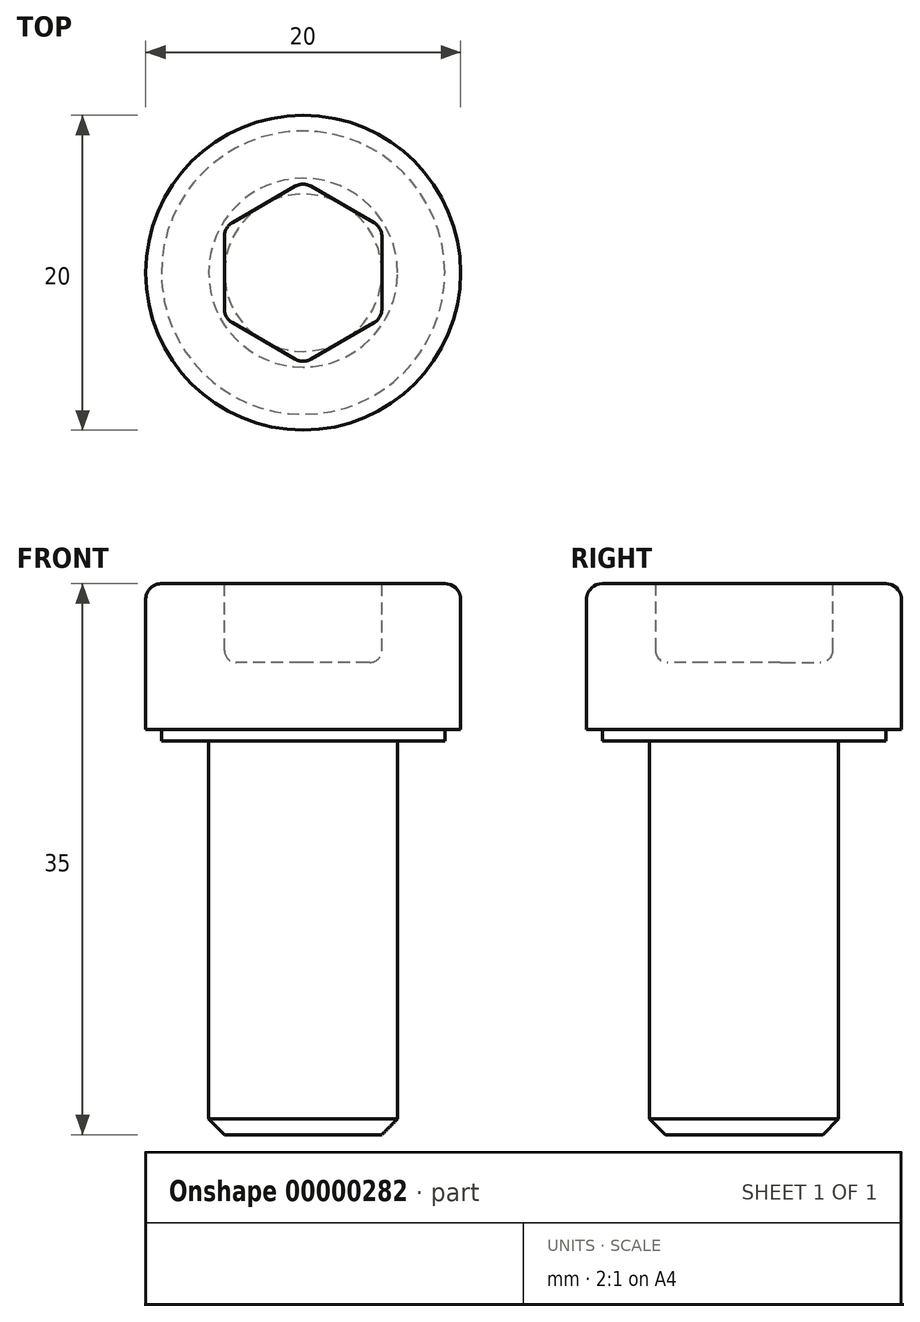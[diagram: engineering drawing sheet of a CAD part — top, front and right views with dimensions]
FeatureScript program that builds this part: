
annotation { "Feature Type Name" : "Feature", "Feature Type Description" : "" }
export const myFeature = defineFeature(function(context is Context, id is Id, definition is map)
    precondition{}
    {
        {
            var Q0;
            Q0 = qCreatedBy(makeId("Front.planeOp"), FACE);
            var sketch = newSketch(context, id + "F0", { "sketchPlane" : qUnion([Q0])});
            skLineSegment(sketch, "E0", {"start": v(-6, 0) * mm, "end": v(-9, 0) * mm});
            skLineSegment(sketch, "E1", {"start": v(-9, 0) * mm, "end": v(-9, 0.75) * mm});
            skLineSegment(sketch, "E2", {"start": v(-9, 0.75) * mm, "end": v(-10, 0.75) * mm});
            skLineSegment(sketch, "E3", {"start": v(-10, 0.75) * mm, "end": v(-10, 10) * mm});
            skLineSegment(sketch, "E4", {"start": v(-10, 10) * mm, "end": v(0, 10) * mm});
            skLineSegment(sketch, "E5", {"start": v(0, 10) * mm, "end": v(0, -25) * mm});
            skLineSegment(sketch, "E6", {"start": v(0, -25) * mm, "end": v(-6, -25) * mm});
            skLineSegment(sketch, "E7", {"start": v(-6, -25) * mm, "end": v(-6, 0) * mm});
            skLineSegment(sketch, "E8", {"start": v(0, -25) * mm, "end": v(0, -26.5) * mm, "construction": true});
            skLineSegment(sketch, "E9.0.MirrorCS", {"start": v(0, -25) * mm, "end": v(6, -25) * mm, "construction": true});
            skLineSegment(sketch, "E10.0.MirrorCS", {"start": v(6, -25) * mm, "end": v(6, 0) * mm, "construction": true});
            skLineSegment(sketch, "E11.0.MirrorCS", {"start": v(6, 0) * mm, "end": v(9, 0) * mm, "construction": true});
            skLineSegment(sketch, "E12.0.MirrorCS", {"start": v(9, 0) * mm, "end": v(9, 0.75) * mm, "construction": true});
            skLineSegment(sketch, "E13.0.MirrorCS", {"start": v(9, 0.75) * mm, "end": v(10, 0.75) * mm, "construction": true});
            skLineSegment(sketch, "E14.0.MirrorCS", {"start": v(10, 0.75) * mm, "end": v(10, 10) * mm, "construction": true});
            skLineSegment(sketch, "E15.0.MirrorCS", {"start": v(10, 10) * mm, "end": v(0, 10) * mm, "construction": true});
            skSolve(sketch);
        }
        {
            var Q0;
            Q0=makeQuery(id+"F0.imprint","IMPRINT",FACE,{"disambiguationData":[TD([[makeQuery(id+"F0.imprint","IMPRINT",EDGE,{"derivedFrom":sQuery(id+"F0.wireOp",EDGE,"E0")}),-1.0]])]});
            var Q1;
            Q1=sQuery(id+"F0.wireOp",EDGE,"E5");
            revolve(context, id + "F1", {"entities" : qUnion([Q0]), "axis" : qUnion([Q1]), "revolveType" : RevolveType.FULL});
        }
        {
            var Q0;
            Q0=makeQuery(id+"F1.opRevolve","SWEPT_FACE",FACE,{"disambiguationData":[OSD([sQuery(id+"F0.wireOp",EDGE,"E4")])]});
            var sketch = newSketch(context, id + "F2", { "sketchPlane" : qUnion([Q0])});
            skCircle(sketch, "E16", {"center": v(0, 0) * mm, "radius": 5.77 * mm, "construction": true});
            skLineSegment(sketch, "E17", {"start": v(0, 5.77) * mm, "end": v(-5, 2.89) * mm});
            skLineSegment(sketch, "E18", {"start": v(-5, 2.89) * mm, "end": v(-5, -2.89) * mm});
            skLineSegment(sketch, "E19", {"start": v(-5, -2.89) * mm, "end": v(0, -5.77) * mm});
            skLineSegment(sketch, "E20", {"start": v(0, -5.77) * mm, "end": v(5, -2.89) * mm});
            skLineSegment(sketch, "E21", {"start": v(5, -2.89) * mm, "end": v(5, 2.89) * mm});
            skLineSegment(sketch, "E22", {"start": v(5, 2.89) * mm, "end": v(0, 5.77) * mm});
            skSolve(sketch);
        }
        {
            var Q0;
            Q0=makeQuery(id+"F2.imprint","IMPRINT",FACE,{"disambiguationData":[TD([[makeQuery(id+"F2.imprint","IMPRINT",EDGE,{"derivedFrom":sQuery(id+"F2.wireOp",EDGE,"E17")}),1.0]])]});
            extrude(context, id + "F3", {"entities" : qUnion([Q0]), "operationType" : NewBodyOperationType.REMOVE, "oppositeDirection" : true, "depth" : 5 * mm});
        }
        {
            var Q0;
            Q0=makeQuery(id+"F1.opRevolve","SWEPT_EDGE",EDGE,{"disambiguationData":[OSD([sQuery(id+"F0.wireOp",EDGE,"E3"),sQuery(id+"F0.wireOp",EDGE,"E4")])]});
            fillet(context, id + "F4", {"entities" : qUnion([Q0]), "radius" : 1 * mm, "tangentPropagation" : true, "allowEdgeOverflow" : false});
        }
        {
            var Q0;
            Q0=makeQuery(id+"F1.opRevolve","SWEPT_EDGE",EDGE,{"disambiguationData":[OSD([sQuery(id+"F0.wireOp",EDGE,"E6"),sQuery(id+"F0.wireOp",EDGE,"E7")])]});
            chamfer(context, id + "F5", {"entities" : qUnion([Q0]), "width" : 1 * mm, "tangentPropagation" : true});
        }
        {
            var Q0;
            Q0=makeQuery(id+"F3.boolean.opBoolean","COPY",EDGE,{"derivedFrom":makeQuery(id+"F3.opExtrude","SWEPT_EDGE",EDGE,{"disambiguationData":[OSD([sQuery(id+"F2.wireOp",EDGE,"E17"),sQuery(id+"F2.wireOp",EDGE,"E22")])]})});
            var Q1;
            Q1=makeQuery(id+"F3.boolean.opBoolean","COPY",EDGE,{"derivedFrom":makeQuery(id+"F3.opExtrude","SWEPT_EDGE",EDGE,{"disambiguationData":[OSD([sQuery(id+"F2.wireOp",EDGE,"E17"),sQuery(id+"F2.wireOp",EDGE,"E18")])]})});
            var Q2;
            Q2=makeQuery(id+"F3.boolean.opBoolean","COPY",EDGE,{"derivedFrom":makeQuery(id+"F3.opExtrude","SWEPT_EDGE",EDGE,{"disambiguationData":[OSD([sQuery(id+"F2.wireOp",EDGE,"E18"),sQuery(id+"F2.wireOp",EDGE,"E19")])]})});
            var Q3;
            Q3=makeQuery(id+"F3.boolean.opBoolean","COPY",EDGE,{"derivedFrom":makeQuery(id+"F3.opExtrude","SWEPT_EDGE",EDGE,{"disambiguationData":[OSD([sQuery(id+"F2.wireOp",EDGE,"E19"),sQuery(id+"F2.wireOp",EDGE,"E20")])]})});
            var Q4;
            Q4=makeQuery(id+"F3.boolean.opBoolean","COPY",EDGE,{"derivedFrom":makeQuery(id+"F3.opExtrude","SWEPT_EDGE",EDGE,{"disambiguationData":[OSD([sQuery(id+"F2.wireOp",EDGE,"E20"),sQuery(id+"F2.wireOp",EDGE,"E21")])]})});
            var Q5;
            Q5=makeQuery(id+"F3.boolean.opBoolean","COPY",EDGE,{"derivedFrom":makeQuery(id+"F3.opExtrude","SWEPT_EDGE",EDGE,{"disambiguationData":[OSD([sQuery(id+"F2.wireOp",EDGE,"E21"),sQuery(id+"F2.wireOp",EDGE,"E22")])]})});
            fillet(context, id + "F6", {"entities" : qUnion([Q0, Q1, Q2, Q3, Q4, Q5]), "radius" : 1 * mm, "tangentPropagation" : true, "allowEdgeOverflow" : false});
        }
        {
            var Q0;
            Q0=makeQuery(id+"F3.boolean.opBoolean","COPY",FACE,{"derivedFrom":makeQuery(id+"F3.opExtrude","CAP_FACE",FACE,{"disambiguationData":[OSD([sQuery(id+"F2.wireOp",EDGE,"E17"),sQuery(id+"F2.wireOp",EDGE,"E18"),sQuery(id+"F2.wireOp",EDGE,"E19"),sQuery(id+"F2.wireOp",EDGE,"E20"),sQuery(id+"F2.wireOp",EDGE,"E21"),sQuery(id+"F2.wireOp",EDGE,"E22")])],"isStart":false})});
            fillet(context, id + "F7", {"entities" : qUnion([Q0]), "radius" : 0.75 * mm, "tangentPropagation" : true, "allowEdgeOverflow" : false});
        }
    });
